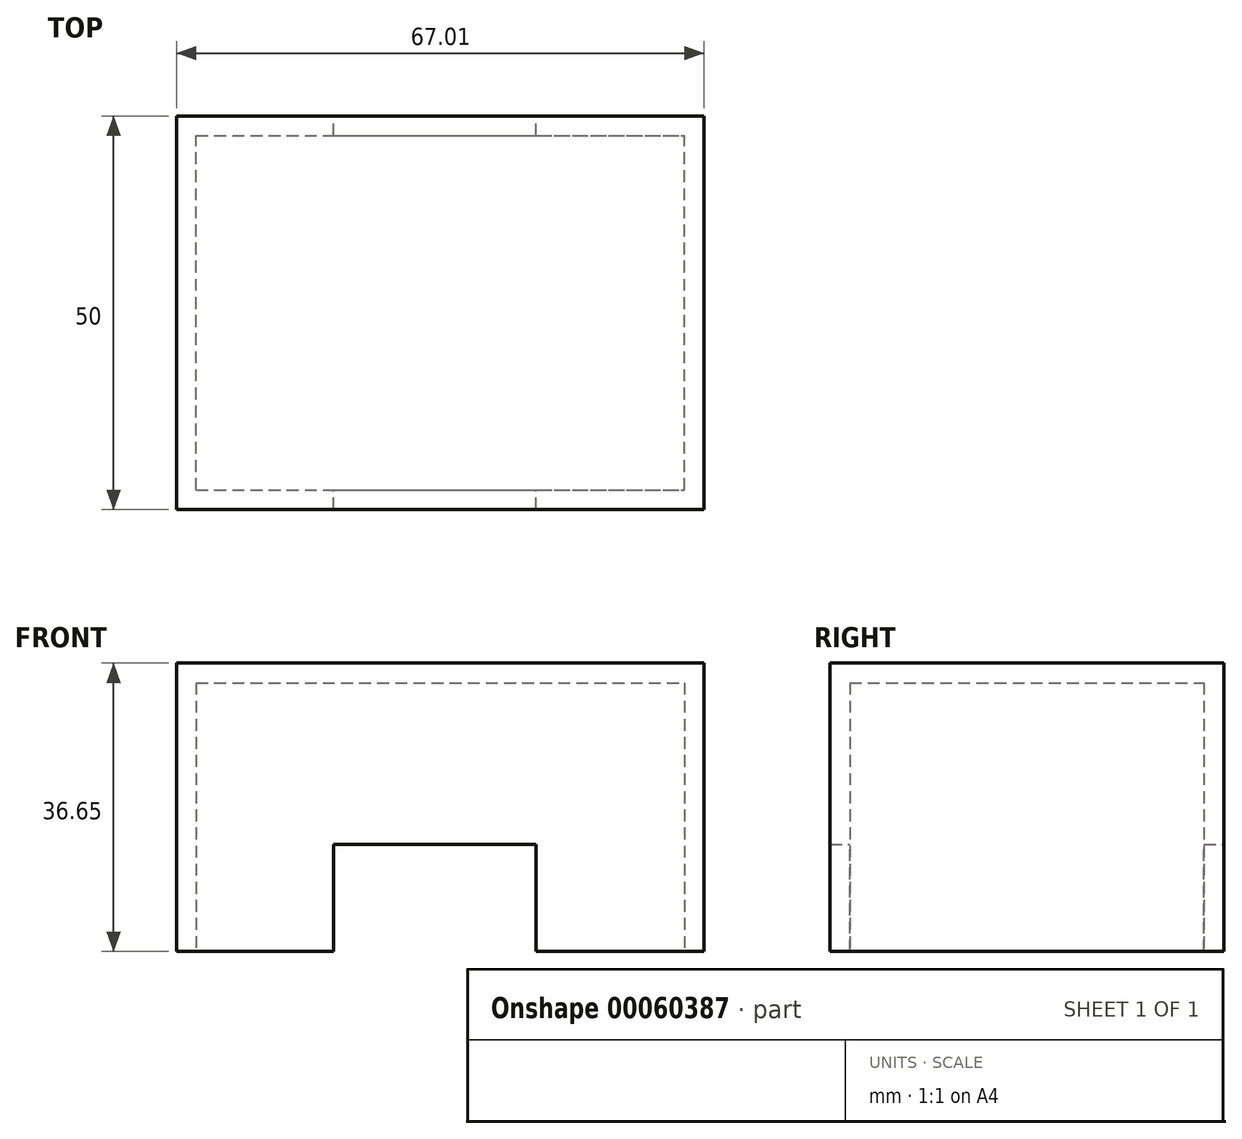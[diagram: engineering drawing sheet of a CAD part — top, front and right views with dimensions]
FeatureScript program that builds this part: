
annotation { "Feature Type Name" : "Feature", "Feature Type Description" : "" }
export const myFeature = defineFeature(function(context is Context, id is Id, definition is map)
    precondition{}
    {
        {
            var Q0;
            Q0=qCreatedBy(makeId("Front.planeOp"),FACE);
            var sketch = newSketch(context, id + "F0", { "sketchPlane" : qUnion([Q0])});
            skLineSegment(sketch, "E0.bottom", {"start": v(-33.24, 23) * mm, "end": v(33.77, 23) * mm});
            skLineSegment(sketch, "E0.top", {"start": v(-33.24, -13.64) * mm, "end": v(-13.28, -13.64) * mm});
            skLineSegment(sketch, "E0.left", {"start": v(-33.24, 23) * mm, "end": v(-33.24, -13.64) * mm});
            skLineSegment(sketch, "E0.right", {"start": v(33.77, 23) * mm, "end": v(33.77, -13.64) * mm});
            skLineSegment(sketch, "E1.top", {"start": v(-13.28, 0) * mm, "end": v(12.43, 0) * mm});
            skLineSegment(sketch, "E1.left", {"start": v(-13.28, -13.64) * mm, "end": v(-13.28, 0) * mm});
            skLineSegment(sketch, "E1.right", {"start": v(12.43, -13.64) * mm, "end": v(12.43, 0) * mm});
            skLineSegment(sketch, "E2.trimOffspring", {"start": v(12.43, -13.64) * mm, "end": v(33.77, -13.64) * mm});
            skSolve(sketch);
        }
        {
            var Q0;
            Q0=makeQuery(id+"F0.imprint","IMPRINT",FACE,{"disambiguationData":[TD([[makeQuery(id+"F0.imprint","IMPRINT",EDGE,{"derivedFrom":sQuery(id+"F0.wireOp",EDGE,"E0.bottom")}),-1.0]])]});
            extrude(context, id + "F1", {"entities" : qUnion([Q0]), "endBound" : BoundingType.SYMMETRIC, "depth" : 50 * mm});
        }
        {
            var Q0;
            Q0=makeQuery(id+"F1.opExtrude","SWEPT_FACE",FACE,{"disambiguationData":[OSD([sQuery(id+"F0.wireOp",EDGE,"E1.top")])]});
            var Q1;
            Q1=makeQuery(id+"F1.opExtrude","SWEPT_FACE",FACE,{"disambiguationData":[OSD([sQuery(id+"F0.wireOp",EDGE,"E2.trimOffspring")])]});
            var Q2;
            Q2=makeQuery(id+"F1.opExtrude","SWEPT_FACE",FACE,{"disambiguationData":[OSD([sQuery(id+"F0.wireOp",EDGE,"E0.top")])]});
            var Q3;
            Q3=makeQuery(id+"F1.opExtrude","SWEPT_FACE",FACE,{"disambiguationData":[OSD([sQuery(id+"F0.wireOp",EDGE,"E1.left")])]});
            var Q4;
            Q4=makeQuery(id+"F1.opExtrude","SWEPT_FACE",FACE,{"disambiguationData":[OSD([sQuery(id+"F0.wireOp",EDGE,"E1.right")])]});
            shell(context, id + "F2", {"entities" : qUnion([Q0, Q1, Q2, Q3, Q4]), "thickness" : 2.5 * mm});
        }
    });
